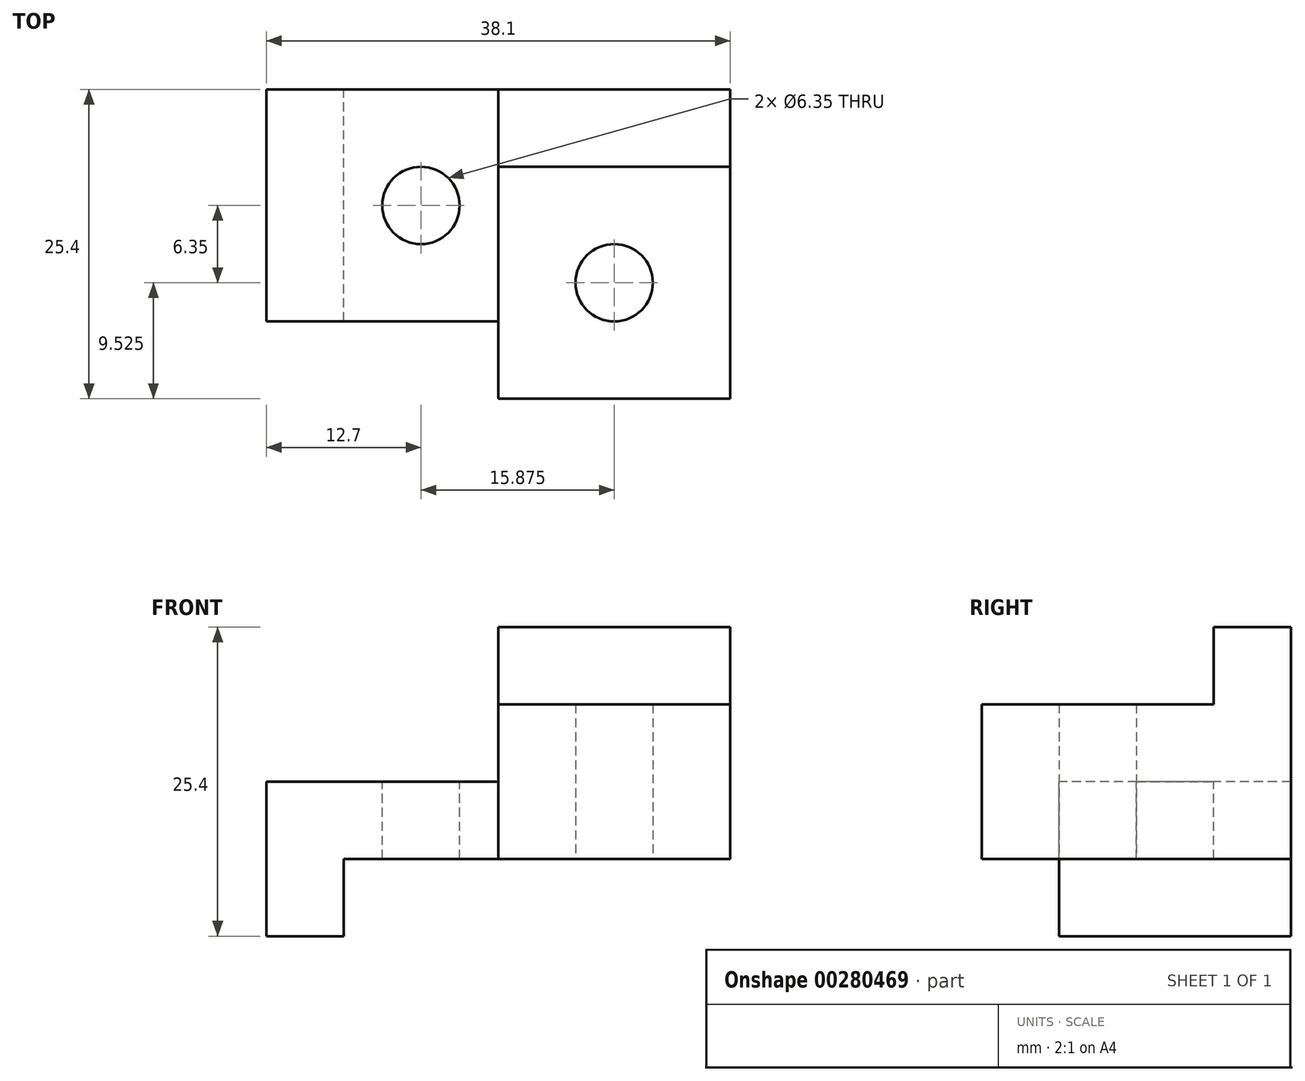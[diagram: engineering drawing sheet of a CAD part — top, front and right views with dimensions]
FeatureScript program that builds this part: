
annotation { "Feature Type Name" : "Feature", "Feature Type Description" : "" }
export const myFeature = defineFeature(function(context is Context, id is Id, definition is map)
    precondition{}
    {
        {
            var Q0;
            Q0=qCreatedBy(makeId("Top.planeOp"),FACE);
            var sketch = newSketch(context, id + "F0", { "sketchPlane" : qUnion([Q0])});
            skLineSegment(sketch, "E0.bottom", {"start": v(0, 0) * mm, "end": v(19.05, 0) * mm});
            skLineSegment(sketch, "E0.top", {"start": v(0, 25.4) * mm, "end": v(19.05, 25.4) * mm});
            skLineSegment(sketch, "E0.left", {"start": v(0, 0) * mm, "end": v(0, 25.4) * mm});
            skLineSegment(sketch, "E0.right", {"start": v(19.05, 0) * mm, "end": v(19.05, 25.4) * mm});
            skCircle(sketch, "E1", {"center": v(9.52, 9.53) * mm, "radius": 3.18 * mm});
            skSolve(sketch);
        }
        {
            var Q0;
            Q0=makeQuery(id+"F0.imprint","IMPRINT",FACE,{"disambiguationData":[TD([[makeQuery(id+"F0.imprint","IMPRINT",EDGE,{"derivedFrom":sQuery(id+"F0.wireOp",EDGE,"E0.bottom")}),1.0]])]});
            extrude(context, id + "F1", {"entities" : qUnion([Q0]), "depth" : 12.7 * mm});
        }
        {
            var Q0;
            Q0=makeQuery(id+"F1.opExtrude","CAP_FACE",FACE,{"disambiguationData":[OSD([sQuery(id+"F0.wireOp",EDGE,"E0.bottom"),sQuery(id+"F0.wireOp",EDGE,"E0.top"),sQuery(id+"F0.wireOp",EDGE,"E0.left"),sQuery(id+"F0.wireOp",EDGE,"E0.right"),sQuery(id+"F0.wireOp",EDGE,"E1")])],"isStart":false});
            var sketch = newSketch(context, id + "F2", { "sketchPlane" : qUnion([Q0])});
            skLineSegment(sketch, "E2.bottom", {"start": v(0, 25.4) * mm, "end": v(19.05, 25.4) * mm});
            skLineSegment(sketch, "E2.top", {"start": v(0, 19.05) * mm, "end": v(19.05, 19.05) * mm});
            skLineSegment(sketch, "E2.left", {"start": v(0, 25.4) * mm, "end": v(0, 19.05) * mm});
            skLineSegment(sketch, "E2.right", {"start": v(19.05, 25.4) * mm, "end": v(19.05, 19.05) * mm});
            skSolve(sketch);
        }
        {
            var Q0;
            Q0 = qSketchRegion(id + "F2", true);
            extrude(context, id + "F3", {"entities" : qUnion([Q0]), "operationType" : NewBodyOperationType.ADD, "depth" : 6.35 * mm});
        }
        {
            var Q0;
            Q0=makeQuery(id+"F3.boolean.opBoolean","MERGE",FACE,{"derivedFrom":[makeQuery(id+"F1.opExtrude","SWEPT_FACE",FACE,{"disambiguationData":[OSD([sQuery(id+"F0.wireOp",EDGE,"E0.left")])]}),makeQuery(id+"F3.opExtrude","SWEPT_FACE",FACE,{"disambiguationData":[OSD([sQuery(id+"F2.wireOp",EDGE,"E2.left")])]})]});
            var sketch = newSketch(context, id + "F4", { "sketchPlane" : qUnion([Q0])});
            skLineSegment(sketch, "E3.bottom", {"start": v(-25.4, 0) * mm, "end": v(-6.35, 0) * mm});
            skLineSegment(sketch, "E3.top", {"start": v(-25.4, 6.35) * mm, "end": v(-6.35, 6.35) * mm});
            skLineSegment(sketch, "E3.left", {"start": v(-25.4, 0) * mm, "end": v(-25.4, 6.35) * mm});
            skLineSegment(sketch, "E3.right", {"start": v(-6.35, 0) * mm, "end": v(-6.35, 6.35) * mm});
            skSolve(sketch);
        }
        {
            var Q0;
            Q0 = qSketchRegion(id + "F4", true);
            extrude(context, id + "F5", {"entities" : qUnion([Q0]), "operationType" : NewBodyOperationType.ADD, "depth" : 19.05 * mm});
        }
        {
            var Q0;
            Q0=makeQuery(id+"F5.opExtrude","SWEPT_FACE",FACE,{"disambiguationData":[OSD([sQuery(id+"F4.wireOp",EDGE,"E3.top")])]});
            var sketch = newSketch(context, id + "F6", { "sketchPlane" : qUnion([Q0])});
            skCircle(sketch, "E4", {"center": v(-6.35, 15.88) * mm, "radius": 3.18 * mm});
            skSolve(sketch);
        }
        {
            var Q0;
            Q0 = qSketchRegion(id + "F6", true);
            extrude(context, id + "F7", {"entities" : qUnion([Q0]), "operationType" : NewBodyOperationType.REMOVE, "endBound" : BoundingType.THROUGH_ALL, "oppositeDirection" : true, "depth" : 25.4 * mm});
        }
        {
            var Q0;
            Q0=makeQuery(id+"F5.boolean.opBoolean","MERGE",FACE,{"derivedFrom":[makeQuery(id+"F1.opExtrude","CAP_FACE",FACE,{"disambiguationData":[OSD([sQuery(id+"F0.wireOp",EDGE,"E0.bottom"),sQuery(id+"F0.wireOp",EDGE,"E0.top"),sQuery(id+"F0.wireOp",EDGE,"E0.left"),sQuery(id+"F0.wireOp",EDGE,"E0.right"),sQuery(id+"F0.wireOp",EDGE,"E1")])],"isStart":true}),makeQuery(id+"F5.opExtrude","SWEPT_FACE",FACE,{"disambiguationData":[OSD([sQuery(id+"F4.wireOp",EDGE,"E3.bottom")])]})]});
            var sketch = newSketch(context, id + "F8", { "sketchPlane" : qUnion([Q0])});
            skLineSegment(sketch, "E5.bottom", {"start": v(-19.05, -6.35) * mm, "end": v(-12.7, -6.35) * mm});
            skLineSegment(sketch, "E5.top", {"start": v(-19.05, -25.4) * mm, "end": v(-12.7, -25.4) * mm});
            skLineSegment(sketch, "E5.left", {"start": v(-19.05, -6.35) * mm, "end": v(-19.05, -25.4) * mm});
            skLineSegment(sketch, "E5.right", {"start": v(-12.7, -6.35) * mm, "end": v(-12.7, -25.4) * mm});
            skSolve(sketch);
        }
        {
            var Q0;
            Q0 = qSketchRegion(id + "F8", true);
            extrude(context, id + "F9", {"entities" : qUnion([Q0]), "operationType" : NewBodyOperationType.ADD, "depth" : 6.35 * mm});
        }
    });
